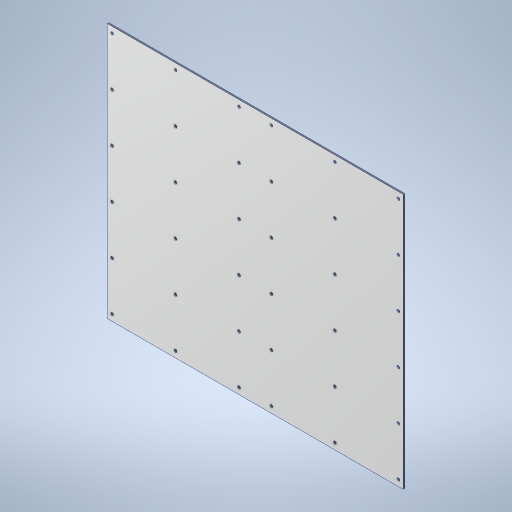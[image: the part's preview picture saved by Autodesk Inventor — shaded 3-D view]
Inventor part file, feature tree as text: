
AUTODESK INVENTOR PART (.ipt)
format: ipt  version: 2024 (Build 280153000, 153)  size: 349,696 bytes
history: native  units: mm
features: sketch x4, extrude x3, other x2, hole x1
ambient origin geometry x8: Origin, YZ Plane, XZ Plane, XY Plane, X Axis, Y Axis, Z Axis, Center Point
bodies: Body1 (feature_tree), Body2 (feature_tree)
feature tree (10):
  other  "Laminate"
  sketch  "Sketch1"  dims[d0=548.0mm d1=473.0mm]
  extrude  "Extrusion1"  Depth=473.0mm
  extrude  "Extrusion2"  Depth=2.9mm TaperAngle=0.0deg
  extrude  "Extrusion3"  Depth=2.9mm
  hole  "Hole4"  [1 undecoded]
  sketch  "Sketch Driven Pattern1"  dims[d2=3.0mm d3=0.0mm d4=2.9mm d5=0.0mm]
  other  "Core"
  sketch  "Sketch6"  dims[d6=2.9mm d7=0.0mm d47=60.0mm]
  sketch  "Sketch8"  dims[d48=450.0mm d49=530.0mm d50=60.0mm d52=90.0mm d53=10.0mm d55=10.0mm d57=5.3mm d58=10.0mm d59=4.0mm d60=2.0mm d61=90.0deg d62=8.0mm d63=20.594885mm d64=265.0mm d65=265.0mm d66=30.0mm d67=30.0mm d69=147.5mm d70=147.5mm]
note: 1 required parameter value undecoded (feature->parameter linkage not recoverable at this tier; creation-order binding heuristic only, values carry confidence <= 0.55)
